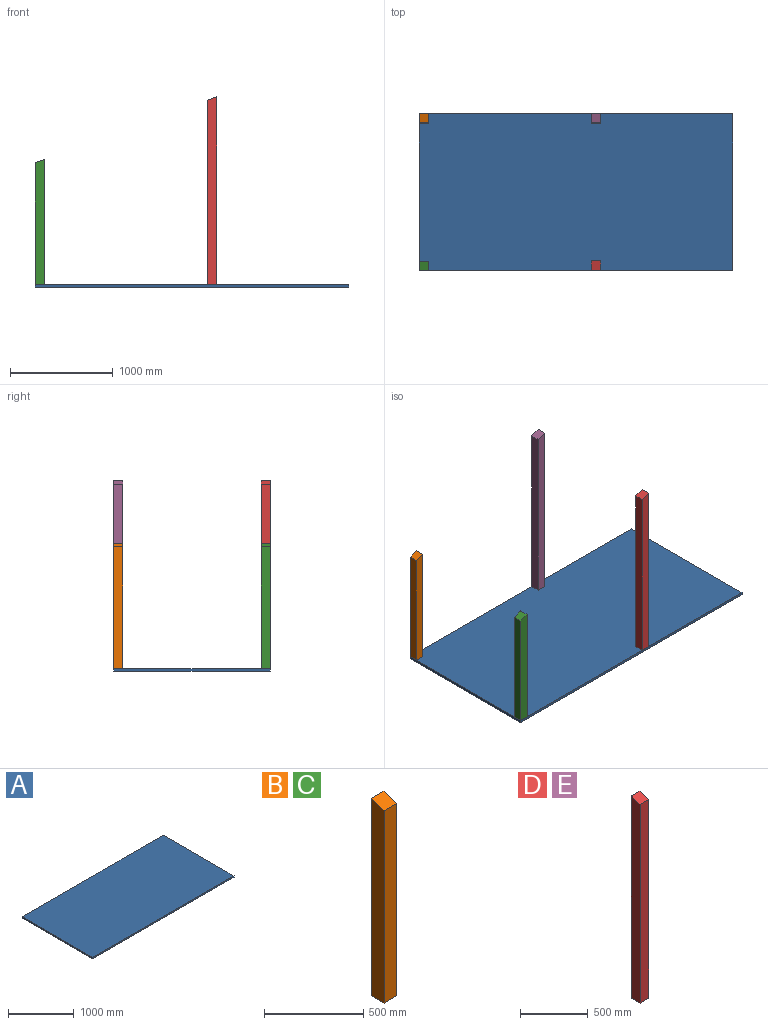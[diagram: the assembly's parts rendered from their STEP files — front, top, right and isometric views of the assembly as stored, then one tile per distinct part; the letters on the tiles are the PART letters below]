
ASSEMBLY  parts=5 mates=11
PART A: 6 faces, bbox 3048x1524x25.4 mm
  f0: plane 1524x25.4mm, normal (-1,0,0), area 38709.6mm2, adj f1,f3,f4,f5
  f1: plane 3048x25.4mm, normal (0,-1,0), area 77419.2mm2, adj f0,f2,f4,f5
  f2: plane 1524x25.4mm, normal (1,0,0), area 38709.6mm2, adj f1,f3,f4,f5
  f3: plane 3048x25.4mm, normal (0,1,0), area 77419.2mm2, adj f0,f2,f4,f5
  f4: plane 3048x1524mm, normal (0,0,1), area 4645152mm2, adj f0,f1,f2,f3
  f5: plane 3048x1524mm, normal (0,0,-1), area 4645152mm2, adj f0,f1,f2,f3
PART B: 6 faces, bbox 88.9x88.9x1219.2 mm
  f0: plane 1219.2x88.9mm, normal (1,0,0), area 106948.6mm2, adj f1,f3,f4,f5
  f1: plane 1219.2x88.9mm, normal (0,1,0), area 108386.9mm2, adj f0,f2,f4,f5
  f2: plane 1219.2x88.9mm, normal (-1,0,0), area 106948.6mm2, adj f1,f3,f4,f5
  f3: plane 1186.84x88.9mm, normal (0,-1,0), area 105510.3mm2, adj f0,f2,f4,f5
  f4: plane 88.9x88.9mm, normal (0,0,-1), area 7903.2mm2, adj f0,f1,f2,f3
  f5: plane 88.9x88.9mm, normal (0,-0.34,0.94), area 8410.4mm2, adj f0,f1,f2,f3
PART C: same geometry as B
PART D: 6 faces, bbox 88.9x88.9x1828.8 mm
  f0: plane 1828.8x88.9mm, normal (1,0,0), area 161142.1mm2, adj f1,f3,f4,f5
  f1: plane 1828.8x88.9mm, normal (0,1,0), area 162580.3mm2, adj f0,f2,f4,f5
  f2: plane 1828.8x88.9mm, normal (-1,0,0), area 161142.1mm2, adj f1,f3,f4,f5
  f3: plane 1796.44x88.9mm, normal (0,-1,0), area 159703.8mm2, adj f0,f2,f4,f5
  f4: plane 88.9x88.9mm, normal (0,0,-1), area 7903.2mm2, adj f0,f1,f2,f3
  f5: plane 88.9x88.9mm, normal (0,-0.34,0.94), area 8410.4mm2, adj f0,f1,f2,f3
PART E: same geometry as D
PLACE A at identity fixed
PLACE B rot(axis=(0,0,-1),90deg) t=(44.45,1479.55,25.4)mm
PLACE C rot(axis=(0,0,-1),90deg) t=(44.45,44.45,25.4)mm
PLACE D rot(axis=(0,0,-1),90deg) t=(1719.31,44.45,25.4)mm
PLACE E rot(axis=(0,0,-1),90deg) t=(1719.31,1479.55,25.4)mm
MATE planar A.f4 <-> D.f4  axis (0,0,1) through (1524,762,25.4)mm
MATE planar A.f4 <-> B.f4  axis (0,0,1) through (1524,762,25.4)mm
MATE planar A.f4 <-> C.f4  axis (0,0,1) through (1524,762,25.4)mm
MATE planar A.f0 <-> B.f3  axis (-1,0,0) through (0,762,12.7)mm
MATE planar A.f0 <-> C.f3  axis (-1,0,0) through (0,762,12.7)mm
MATE planar B.f2 <-> A.f3  axis (0,1,0) through (44.45,1524,635)mm
MATE planar E.f5 <-> B.f5  axis (-0.34,0,0.94) through (1719.31,1479.55,1838.02)mm
MATE planar E.f2 <-> A.f3  axis (0,1,0) through (1719.31,1524,939.8)mm
MATE planar E.f4 <-> A.f4  axis (0,0,-1) through (1719.31,1479.55,25.4)mm
MATE planar D.f5 <-> C.f5  axis (-0.34,0,0.94) through (1719.31,44.45,1838.02)mm
MATE planar A.f1 <-> C.f0  axis (0,-1,0) through (1524,0,12.7)mm
